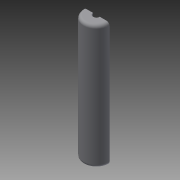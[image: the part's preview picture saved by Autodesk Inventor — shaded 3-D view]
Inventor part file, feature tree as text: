
AUTODESK INVENTOR PART (.ipt)
format: ipt  version: 2014 (Build 180170000, 170)  size: 359,936 bytes
history: native  units: mm
features: sketch x4, extrude x3, fillet x1, emboss x1
ambient origin geometry x8: Origin, YZ Plane, XZ Plane, XY Plane, X Axis, Y Axis, Z Axis, Center Point
bodies: Solid1 (feature_tree)
feature tree (9):
  extrude  "Extrusion1"  Depth=6.604mm
  fillet  "Fillet1"  Radius=120.65mm
  extrude  "Extrusion2"  TaperAngle=0.0deg  [1 undecoded]
  extrude  "Extrusion3"  Depth=11.5062mm
  emboss  "Emboss1"
  sketch  "Sketch1"  dims[d0=25.4mm d1=6.604mm d2=120.65mm d3=0.0mm]
  sketch  "Sketch3"  dims[d4=3.0mm d5=0.0mm d6=0.0mm]
  sketch  "Sketch4"  dims[d7=17.653mm d8=11.5062mm]
  sketch  "Sketch7"  dims[d9=9.0mm d10=0.0mm d11=3.0mm d12=1.0mm d13=1.0mm d14=2.0mm d15=0.0mm d16=60.325mm d17=25.4mm d18=25.4mm]
note: 1 required parameter value undecoded (feature->parameter linkage not recoverable at this tier; creation-order binding heuristic only, values carry confidence <= 0.55)
